# Revit family: KR6040001_ Canastilla Ducha Koral
name_source: partatom
category: Furniture
units: mm (PartAtom-declared; Revit-internal decimal feet)

## family parameters
Always vertical = Yes
Cut with Voids When Loaded = No
Host = Wall
OmniClass Number = 23.31.25.29.11
OmniClass Title = Hand Soap Holders
Room Calculation Point = No
Shared = No

## types (1)
- Type 1
    Alto = 800 mm  [stored 2.62467 ft]
    Colección = Koral
    Creado por = BIMBAU
    Default Elevation = 0 mm  [stored 0 ft]
    Description = La jabonera ducha Koral es combinable con las demás piezas de la linea de accesorios y cuenta con sistema de fijación oculto justo lo que buscabas. ¡Conócela ahora!
    Fecha de creación = 07/04/2021
    Garantía = 30 años en estructura
    Manufacturer = Corona
    Material = Corona_Cromado
    Referencia = KR6040001
    Resistencia = Resistente a la corrosión, pelado y decoloración por agua

note: [stored X ft] marks values corroborated as IEEE doubles in the binary element streams (Revit-internal decimal feet)

## geometry (parser evidence)
native form markers: Sweep x3
no freeform markers — native parametric forms only
